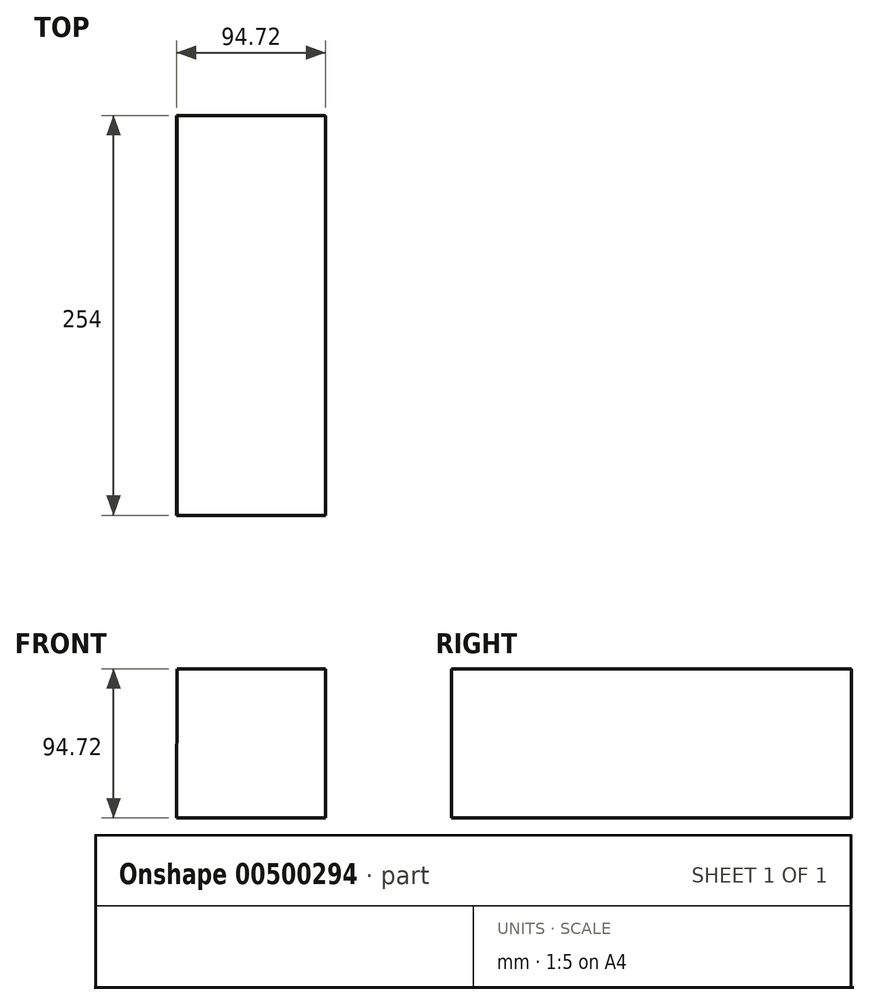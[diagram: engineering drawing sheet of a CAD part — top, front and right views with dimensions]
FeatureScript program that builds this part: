
annotation { "Feature Type Name" : "Feature", "Feature Type Description" : "" }
export const myFeature = defineFeature(function(context is Context, id is Id, definition is map)
    precondition{}
    {
        {
            var Q0;
            Q0=qCreatedBy(makeId("Front.planeOp"),FACE);
            var sketch = newSketch(context, id + "F0", { "sketchPlane" : qUnion([Q0])});
            skCircle(sketch, "E0.cCircle", {"center": v(0, 0) * mm, "radius": 66.88 * mm, "construction": true});
            skLineSegment(sketch, "E0.0", {"start": v(-47.22, 47.36) * mm, "end": v(47.36, 47.22) * mm});
            skLineSegment(sketch, "E0.1", {"start": v(47.36, 47.22) * mm, "end": v(47.22, -47.36) * mm});
            skLineSegment(sketch, "E0.2", {"start": v(47.22, -47.36) * mm, "end": v(-47.36, -47.22) * mm});
            skLineSegment(sketch, "E0.3", {"start": v(-47.36, -47.22) * mm, "end": v(-47.22, 47.36) * mm});
            skSolve(sketch);
        }
        {
            var Q0;
            Q0=makeQuery(id+"F0.imprint","IMPRINT",FACE,{"disambiguationData":[TD([[makeQuery(id+"F0.imprint","IMPRINT",EDGE,{"derivedFrom":sQuery(id+"F0.wireOp",EDGE,"E0.0")}),-1.0]])]});
            extrude(context, id + "F1", {"entities" : qUnion([Q0]), "endBound" : BoundingType.SYMMETRIC, "depth" : 254 * mm});
        }
    });
